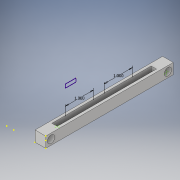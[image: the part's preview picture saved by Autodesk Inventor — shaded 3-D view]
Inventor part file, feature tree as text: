
AUTODESK INVENTOR PART (.ipt)
format: ipt  version: 2018 (Build 220112000, 112)  size: 323,584 bytes
history: native  units: in
note: dims shown in document units (in); Inventor stores cm internally (conversion verified against a paired STEP export)
features: sketch x21, extrude x11, fillet x2, hole x1
ambient origin geometry x8: Origin, YZ Plane, XZ Plane, XY Plane, X Axis, Y Axis, Z Axis, Center Point
bodies: Solid1 (feature_tree)
feature tree (35):
  extrude  "Extrusion1"  Depth=4.5in
  sketch  "Sketch2"  dims[d2=0.375in d3=0.0in d4=0.1875in]
  extrude  "Extrusion2"  Depth=0.1875in
  extrude  "Extrusion3"  Depth=0.375in TaperAngle=0.0deg
  sketch  "Sketch5"  dims[d10=0.325in d11=0.0in d12=0.3625in d13=0.0in]
  extrude  "Extrusion4"  Depth=0.26in
  extrude  "Extrusion5"  Depth=0.3625in TaperAngle=0.0deg
  extrude  "Extrusion6"  Depth=0.26in
  sketch  "Sketch9"  dims[d25=0.25in d26=0.0in d27=0.125in]
  sketch  "Sketch10"  dims[d28=0.125in d29=1.0in]
  extrude  "Extrusion7"  Depth=0.375in
  sketch  "Sketch12"  dims[d33=0.25in d34=0.75in d35=0.375in d36=0.25in d37=0.5635in d38=0.12in d39=0.8108in]
  extrude  "Extrusion8"  Depth=0.75in TaperAngle=0.0deg
  fillet  "Fillet1"  Radius=0.25in
  fillet  "Fillet2"  Radius=0.25in
  sketch  "Sketch14"  dims[d42=0.5in d43=0.0in]
  sketch  "Sketch15"
  sketch  "Sketch16"
  sketch  "Sketch17"
  sketch  "Sketch18"
  sketch  "Sketch19"
  extrude  "Extrusion9"  Depth=0.125in
  hole  "Hole1"  [1 undecoded]
  extrude  "Extrusion10"  Depth=0.125in TaperAngle=0.0deg
  extrude  "Extrusion11"  Depth=0.375in
  sketch  "Sketch1"  dims[d0=0.375in d1=4.5in]
  sketch  "Sketch3"  dims[d5=3.5in d6=0.375in d7=0.0in]
  sketch  "Sketch4"  dims[d8=0.25in d9=0.26in]
  sketch  "Sketch6"  dims[d14=0.26in d15=0.26in]
  sketch  "Sketch7"  dims[d16=0.3in d17=0.0in d18=0.375in]
  sketch  "Sketch8"  dims[d19=0.125in d20=0.75in d21=0.0in d22=0.25in d23=0.0in d24=0.25in]
  sketch  "Sketch11"  dims[d30=1.0in d31=0.125in d32=0.0in]
  sketch  "Sketch13"  dims[d40=1.0in d41=0.0in]
  sketch  "Sketch20"
  sketch  "Sketch21"
note: 1 required parameter value undecoded (feature->parameter linkage not recoverable at this tier; creation-order binding heuristic only, values carry confidence <= 0.55)
